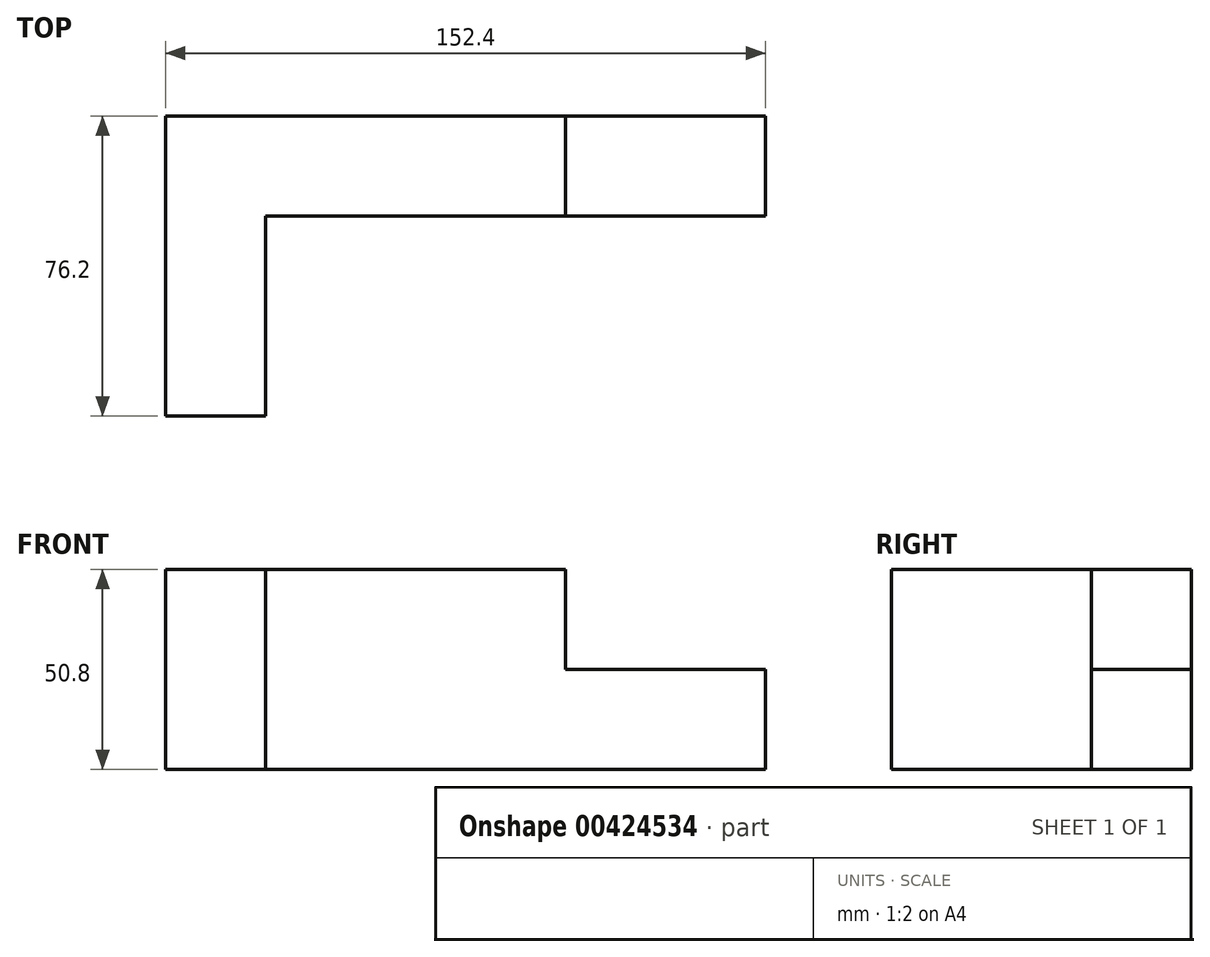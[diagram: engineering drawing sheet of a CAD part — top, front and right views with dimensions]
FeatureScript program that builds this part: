
annotation { "Feature Type Name" : "Feature", "Feature Type Description" : "" }
export const myFeature = defineFeature(function(context is Context, id is Id, definition is map)
    precondition{}
    {
        {
            var Q0;
            Q0=qCreatedBy(makeId("Front.planeOp"),FACE);
            var sketch = newSketch(context, id + "F0", { "sketchPlane" : qUnion([Q0])});
            skLineSegment(sketch, "E0", {"start": v(0, 0) * mm, "end": v(152.4, 0) * mm});
            skLineSegment(sketch, "E1", {"start": v(0, 0) * mm, "end": v(0, 50.8) * mm});
            skLineSegment(sketch, "E2", {"start": v(152.4, 0) * mm, "end": v(152.4, 50.8) * mm});
            skLineSegment(sketch, "E3", {"start": v(0, 50.8) * mm, "end": v(152.4, 50.8) * mm});
            skSolve(sketch);
        }
        {
            var Q0;
            Q0=makeQuery(id+"F0.imprint","IMPRINT",FACE,{"disambiguationData":[TD([[makeQuery(id+"F0.imprint","IMPRINT",EDGE,{"derivedFrom":sQuery(id+"F0.wireOp",EDGE,"E0")}),1.0]])]});
            extrude(context, id + "F1", {"entities" : qUnion([Q0]), "oppositeDirection" : true, "depth" : 76.2 * mm});
        }
        {
            var Q0;
            Q0=qCreatedBy(makeId("Front.planeOp"),FACE);
            var sketch = newSketch(context, id + "F2", { "sketchPlane" : qUnion([Q0])});
            skLineSegment(sketch, "E4", {"start": v(0, 0) * mm, "end": v(25.4, 0) * mm});
            skLineSegment(sketch, "E5", {"start": v(25.4, 0) * mm, "end": v(25.4, 50.8) * mm});
            skLineSegment(sketch, "E6", {"start": v(25.4, 50.8) * mm, "end": v(152.4, 50.8) * mm});
            skLineSegment(sketch, "E7", {"start": v(152.4, 50.8) * mm, "end": v(152.4, 0) * mm});
            skLineSegment(sketch, "E8", {"start": v(152.4, 0) * mm, "end": v(25.4, 0) * mm});
            skSolve(sketch);
        }
        {
            var Q0;
            Q0=makeQuery(id+"F2.imprint","IMPRINT",FACE,{"disambiguationData":[TD([[makeQuery(id+"F2.imprint","IMPRINT",EDGE,{"derivedFrom":sQuery(id+"F2.wireOp",EDGE,"E5")}),-1.0]])]});
            extrude(context, id + "F3", {"entities" : qUnion([Q0]), "operationType" : NewBodyOperationType.REMOVE, "oppositeDirection" : true, "depth" : 50.8 * mm});
        }
        {
            var Q0;
            Q0=qCreatedBy(makeId("Front.planeOp"),FACE);
            var sketch = newSketch(context, id + "F4", { "sketchPlane" : qUnion([Q0])});
            skLineSegment(sketch, "E9", {"start": v(0, 0) * mm, "end": v(152.4, 0) * mm});
            skLineSegment(sketch, "E10", {"start": v(152.4, 0) * mm, "end": v(152.4, 25.4) * mm});
            skLineSegment(sketch, "E11", {"start": v(152.4, 25.4) * mm, "end": v(101.6, 25.4) * mm});
            skLineSegment(sketch, "E12", {"start": v(101.6, 25.4) * mm, "end": v(101.6, 50.8) * mm});
            skLineSegment(sketch, "E13", {"start": v(101.6, 50.8) * mm, "end": v(152.4, 50.8) * mm});
            skLineSegment(sketch, "E14", {"start": v(152.4, 50.8) * mm, "end": v(152.4, 25.4) * mm});
            skSolve(sketch);
        }
        {
            var Q0;
            Q0=makeQuery(id+"F4.imprint","IMPRINT",FACE,{"disambiguationData":[TD([[makeQuery(id+"F4.imprint","IMPRINT",EDGE,{"derivedFrom":sQuery(id+"F4.wireOp",EDGE,"E11")}),-1.0]])]});
            extrude(context, id + "F5", {"entities" : qUnion([Q0]), "operationType" : NewBodyOperationType.REMOVE, "oppositeDirection" : true, "depth" : 76.2 * mm});
        }
    });
